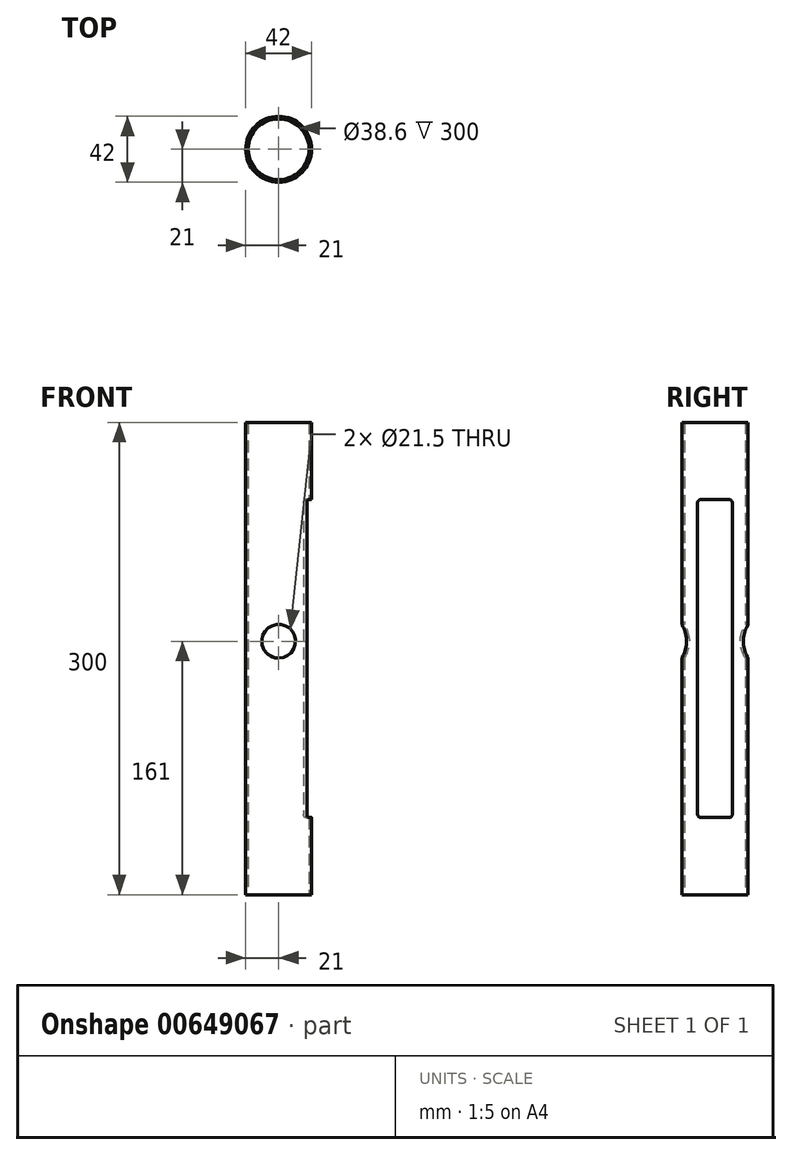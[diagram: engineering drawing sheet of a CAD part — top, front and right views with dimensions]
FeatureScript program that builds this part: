
annotation { "Feature Type Name" : "Feature", "Feature Type Description" : "" }
export const myFeature = defineFeature(function(context is Context, id is Id, definition is map)
    precondition{}
    {
        {
            var Q0;
            Q0=qCreatedBy(makeId("Top.planeOp"),FACE);
            var sketch = newSketch(context, id + "F0", { "sketchPlane" : qUnion([Q0])});
            skCircle(sketch, "E0", {"center": v(0, 0) * mm, "radius": 21 * mm});
            skCircle(sketch, "E1", {"center": v(0, 0) * mm, "radius": 19.3 * mm});
            skSolve(sketch);
        }
        {
            var Q0;
            Q0=makeQuery(id+"F0.imprint","IMPRINT",FACE,{"disambiguationData":[TD([[makeQuery(id+"F0.imprint","IMPRINT",EDGE,{"derivedFrom":sQuery(id+"F0.wireOp",EDGE,"E0")}),1.0]])]});
            var Q1;
            Q1=sQuery(id+"F0.wireOp",EDGE,"E1");
            var Q2;
            Q2=sQuery(id+"F0.wireOp",EDGE,"E0");
            extrude(context, id + "F1", {"entities" : qUnion([Q0]), "surfaceEntities" : qUnion([Q1, Q2]), "endBound" : BoundingType.SYMMETRIC, "depth" : 300 * mm, "offsetDistance" : 25 * mm});
        }
        {
            var Q0;
            Q0=qCreatedBy(makeId("Right.planeOp"),FACE);
            var sketch = newSketch(context, id + "F2", { "sketchPlane" : qUnion([Q0])});
            skLineSegment(sketch, "E2.bottom", {"start": v(9, -101) * mm, "end": v(-9, -101) * mm});
            skLineSegment(sketch, "E2.top", {"start": v(9, 101) * mm, "end": v(-9, 101) * mm});
            skLineSegment(sketch, "E2.left", {"start": v(11, -99) * mm, "end": v(11, 99) * mm});
            skLineSegment(sketch, "E2.right", {"start": v(-11, -99) * mm, "end": v(-11, 99) * mm});
            skPoint(sketch, "E2.middle", {"position": v(0, 0) * mm});
            skPoint(sketch, "E3.visualSharp", {"position": v(-11, 101) * mm});
            skArc(sketch, "E3.filletArc", {"start": v(-9, 101) * mm, "mid": v(-10.41, 100.41) * mm, "end": v(-11, 99) * mm});
            skPoint(sketch, "E4.visualSharp", {"position": v(11, 101) * mm});
            skArc(sketch, "E4.filletArc", {"start": v(11, 99) * mm, "mid": v(10.41, 100.41) * mm, "end": v(9, 101) * mm});
            skPoint(sketch, "E5.visualSharp", {"position": v(11, -101) * mm});
            skArc(sketch, "E5.filletArc", {"start": v(9, -101) * mm, "mid": v(10.41, -100.41) * mm, "end": v(11, -99) * mm});
            skPoint(sketch, "E6.visualSharp", {"position": v(-11, -101) * mm});
            skArc(sketch, "E6.filletArc", {"start": v(-11, -99) * mm, "mid": v(-10.41, -100.41) * mm, "end": v(-9, -101) * mm});
            skSolve(sketch);
        }
        {
            var Q0;
            Q0=makeQuery(id+"F2.imprint","IMPRINT",FACE,{"disambiguationData":[TD([[makeQuery(id+"F2.imprint","IMPRINT",EDGE,{"derivedFrom":sQuery(id+"F2.wireOp",EDGE,"E2.bottom")}),-1.0]])]});
            var Q1;
            Q1=sQuery(id+"F2.wireOp",EDGE,"E5.filletArc");
            var Q2;
            Q2=sQuery(id+"F2.wireOp",EDGE,"E3.filletArc");
            var Q3;
            Q3=sQuery(id+"F2.wireOp",EDGE,"E2.top");
            var Q4;
            Q4=sQuery(id+"F2.wireOp",EDGE,"E2.bottom");
            var Q5;
            Q5=sQuery(id+"F2.wireOp",EDGE,"E2.left");
            var Q6;
            Q6=sQuery(id+"F2.wireOp",EDGE,"E2.right");
            var Q7;
            Q7=sQuery(id+"F2.wireOp",EDGE,"E6.filletArc");
            var Q8;
            Q8=sQuery(id+"F2.wireOp",EDGE,"E4.filletArc");
            extrude(context, id + "F3", {"entities" : qUnion([Q0]), "operationType" : NewBodyOperationType.REMOVE, "surfaceEntities" : qUnion([Q1, Q2, Q3, Q4, Q5, Q6, Q7, Q8]), "endBound" : BoundingType.THROUGH_ALL, "depth" : 25 * mm, "offsetDistance" : 25 * mm});
        }
        {
            var Q0;
            Q0=qCreatedBy(makeId("Front.planeOp"),FACE);
            var sketch = newSketch(context, id + "F4", { "sketchPlane" : qUnion([Q0])});
            skLineSegment(sketch, "E7", {"start": v(0, 0) * mm, "end": v(0, 22) * mm, "construction": true});
            skCircle(sketch, "E8", {"center": v(0, 11) * mm, "radius": 10.75 * mm});
            skSolve(sketch);
        }
        {
            var Q0;
            Q0=makeQuery(id+"F4.imprint","IMPRINT",FACE,{"disambiguationData":[TD([[makeQuery(id+"F4.imprint","IMPRINT",EDGE,{"derivedFrom":sQuery(id+"F4.wireOp",EDGE,"E8")}),1.0]])]});
            extrude(context, id + "F5", {"entities" : qUnion([Q0]), "operationType" : NewBodyOperationType.REMOVE, "endBound" : BoundingType.THROUGH_ALL, "oppositeDirection" : true, "depth" : 25 * mm, "offsetDistance" : 25 * mm, "hasSecondDirection" : true, "secondDirectionBound" : SecondDirectionBoundingType.THROUGH_ALL, "secondDirectionOppositeDirection" : false, "secondDirectionDepth" : 25 * mm});
        }
    });
